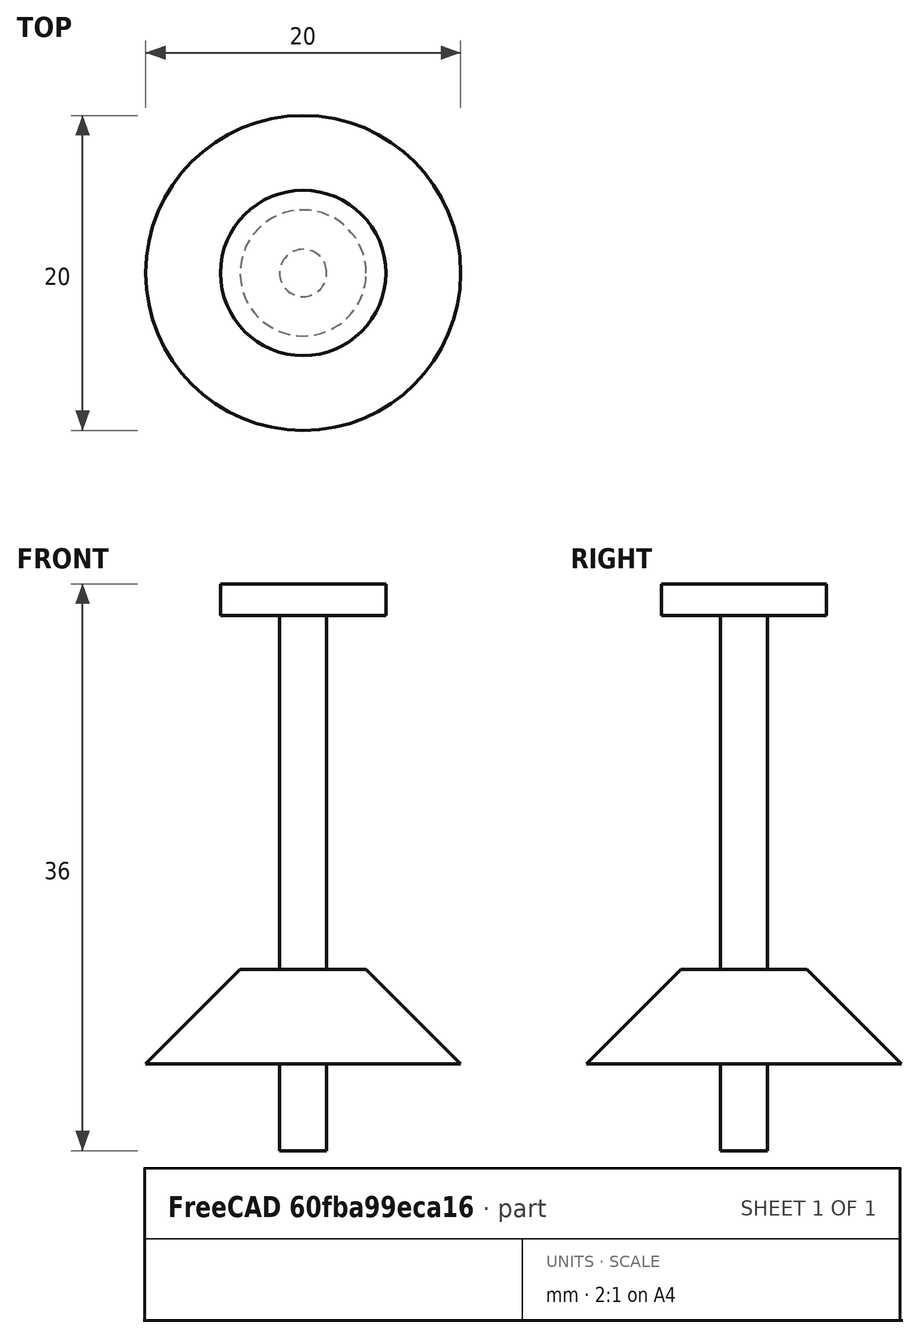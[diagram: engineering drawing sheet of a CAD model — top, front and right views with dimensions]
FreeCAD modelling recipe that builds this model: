
FCSTD DOCUMENT  (FreeCAD 0.14R3700 (Git))
Label: BIRR_axeEntrainement
License: CC-BY 3.0
LicenseURL: http://creativecommons.org/licenses/by/3.0/
objects: Sketcher::SketchObject×1, Part::Revolution×1, Part::Feature×1
note: 3 computed .brp shape members not serialized (recipe doc carries the construction recipe); baked Part::Feature solids carry a one-line shape summary decoded from their .brp

FEATURE [Sketcher::SketchObject] Sketch  label="AxeEntrainement"
  Placement = pos=(0,0,0) rot=(1,0,0;1.5708rad)
  sketch-geometry (10):
    g0: LineSegment StartX=0 StartY=0 StartZ=0 EndX=1.5 EndY=0 EndZ=0
    g1: LineSegment StartX=1.5 StartY=0 StartZ=0 EndX=1.5 EndY=5.5 EndZ=0
    g2: LineSegment StartX=1.5 StartY=5.5 StartZ=0 EndX=10 EndY=5.5 EndZ=0
    g3: LineSegment StartX=10 StartY=5.5 StartZ=0 EndX=4 EndY=11.5 EndZ=0
    g4: LineSegment StartX=1.5 StartY=11.5 StartZ=0 EndX=1.5 EndY=34 EndZ=0
    g5: LineSegment StartX=1.5 StartY=34 StartZ=0 EndX=5.25 EndY=34 EndZ=0
    g6: LineSegment StartX=5.25 StartY=34 StartZ=0 EndX=5.25 EndY=36 EndZ=0
    g7: LineSegment StartX=5.25 StartY=36 StartZ=0 EndX=0 EndY=36 EndZ=0
    g8: LineSegment StartX=0 StartY=36 StartZ=0 EndX=0 EndY=0 EndZ=0
    g9: LineSegment StartX=4 StartY=11.5 StartZ=0 EndX=1.5 EndY=11.5 EndZ=0
  constraints (30):
    c: Coincident(g0,g-1)
    c: Horizontal(g0)
    c: Coincident(g1,g0)
    c: Vertical(g1)
    c: Coincident(g2,g1)
    c: Horizontal(g2)
    c: Coincident(g3,g2)
    c: Vertical(g4)
    c: Coincident(g5,g4)
    c: Horizontal(g5)
    c: Coincident(g6,g5)
    c: Vertical(g6)
    c: Horizontal(g7)
    c: Coincident(g8,g-1)
    c: Vertical(g8)
    c: DistanceX(g-1,g2) = 10
    c: DistanceX(g-1,g0) = 1.5
    c: DistanceY(g6) = 2
    c: DistanceX(g-1,g7) = 5.25
    c: Coincident(g7,g6)
    c: DistanceY(g0,g2) = 5.5
    c: Angle(g3,g2) = 0.785398
    c: DistanceY(g4) = 22.5
    c: Coincident(g8)
    c: Coincident(g8,g7)
    c: Coincident(g9,g3)
    c: Horizontal(g9)
    c: DistanceX(g-1,g4) = 1.5
    c: Coincident(g9,g4)
    c: DistanceY(g1,g4) = 6
FEATURE [Part::Revolution] Revolve
  Angle = 360
  Axis = (0,0,1)
  Base = (0,0,0)
  Solid = false
  Source = -> Sketch
FEATURE [Part::Feature] Revolve001  label="AxeEntrainement_copy"
  shape: bbox 20 x 20 x 36 mm, 9 faces, 0 solids (baked)
